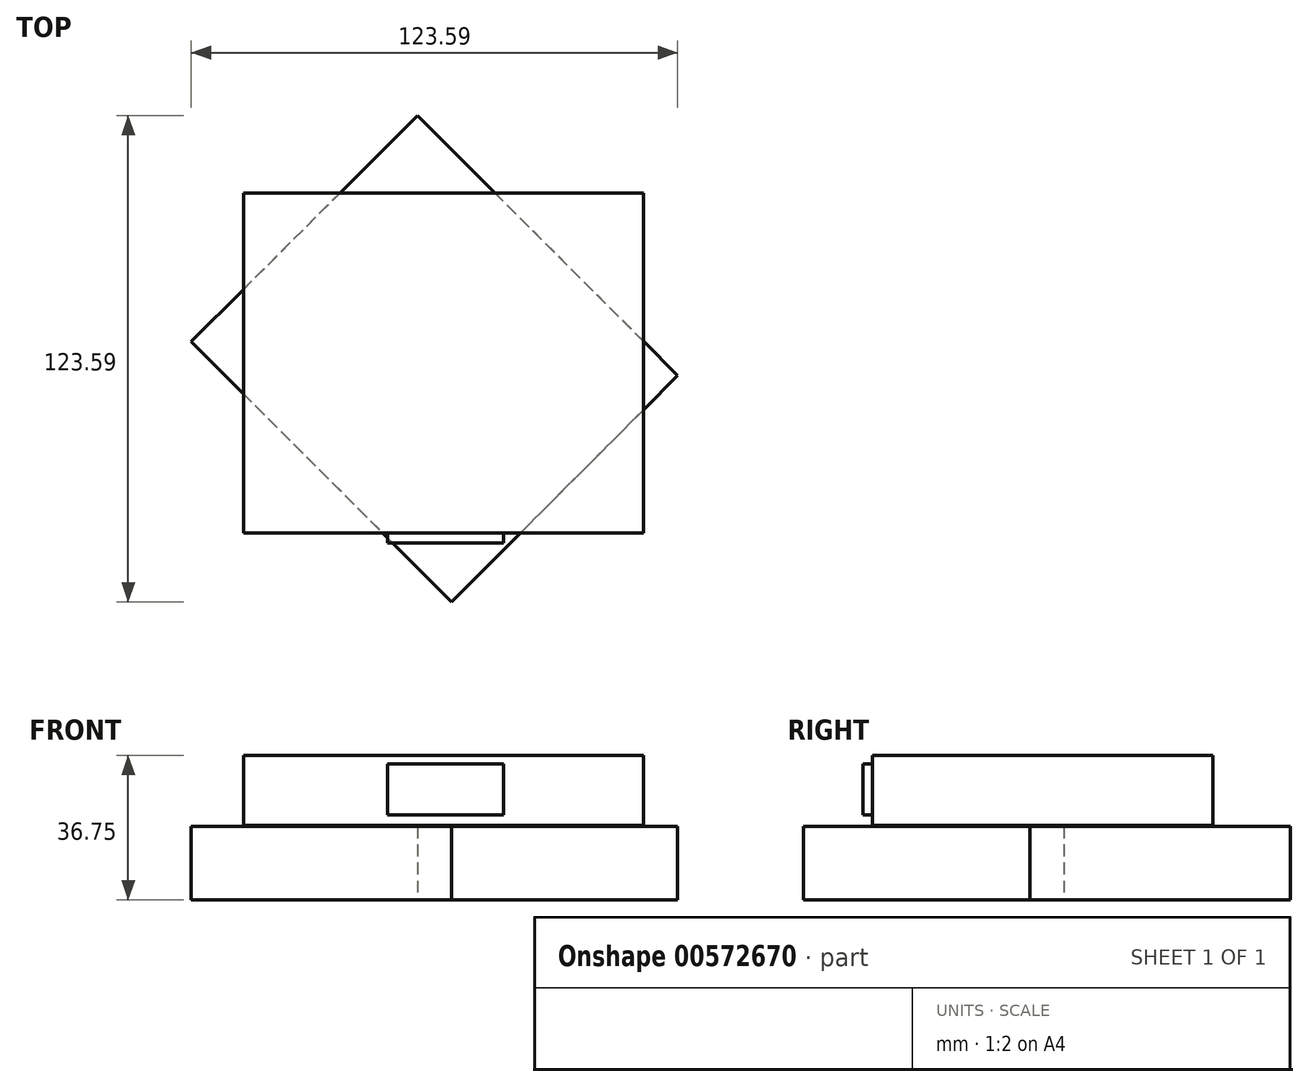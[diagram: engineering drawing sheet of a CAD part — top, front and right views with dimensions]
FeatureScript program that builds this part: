
annotation { "Feature Type Name" : "Feature", "Feature Type Description" : "" }
export const myFeature = defineFeature(function(context is Context, id is Id, definition is map)
    precondition{}
    {
        {
            var Q0;
            Q0=qCreatedBy(makeId("Front.planeOp"),FACE);
            var sketch = newSketch(context, id + "F0", { "sketchPlane" : qUnion([Q0])});
            skLineSegment(sketch, "E0.bottom", {"start": v(-50.88, 9.26) * mm, "end": v(50.72, 9.26) * mm});
            skLineSegment(sketch, "E0.top", {"start": v(-50.88, -8.52) * mm, "end": v(50.72, -8.52) * mm});
            skLineSegment(sketch, "E0.left", {"start": v(-50.88, 9.26) * mm, "end": v(-50.88, -8.52) * mm});
            skLineSegment(sketch, "E0.right", {"start": v(50.72, 9.26) * mm, "end": v(50.72, -8.52) * mm});
            skLineSegment(sketch, "E1", {"start": v(-50.88, -8.52) * mm, "end": v(0, -8.52) * mm});
            skSolve(sketch);
        }
        {
            var Q0;
            Q0=makeQuery(id+"F0.imprint","IMPRINT",FACE,{"disambiguationData":[TD([[makeQuery(id+"F0.imprint","IMPRINT",EDGE,{"derivedFrom":sQuery(id+"F0.wireOp",EDGE,"E0.bottom")}),-1.0]])]});
            extrude(context, id + "F1", {"entities" : qUnion([Q0]), "endBound" : BoundingType.SYMMETRIC, "depth" : 88.9 * mm, "offsetDistance" : 25.4 * mm});
        }
        {
            var Q0;
            Q0=makeQuery(id+"F1.opExtrude","CAP_FACE",FACE,{"disambiguationData":[OSD([sQuery(id+"F0.wireOp",EDGE,"E0.bottom"),sQuery(id+"F0.wireOp",EDGE,"E0.top"),sQuery(id+"F0.wireOp",EDGE,"E0.left"),sQuery(id+"F0.wireOp",EDGE,"E0.right"),sQuery(id+"F0.wireOp",EDGE,"E1")])],"isStart":false});
            var sketch = newSketch(context, id + "F2", { "sketchPlane" : qUnion([Q0])});
            skLineSegment(sketch, "E2.bottom", {"start": v(-14.24, 7.12) * mm, "end": v(15.26, 7.12) * mm});
            skLineSegment(sketch, "E2.top", {"start": v(-14.24, -5.88) * mm, "end": v(15.26, -5.88) * mm});
            skLineSegment(sketch, "E2.left", {"start": v(-14.24, 7.12) * mm, "end": v(-14.24, -5.88) * mm});
            skLineSegment(sketch, "E2.right", {"start": v(15.26, 7.12) * mm, "end": v(15.26, -5.88) * mm});
            skSolve(sketch);
        }
        {
            var Q0;
            Q0=makeQuery(id+"F2.imprint","IMPRINT",FACE,{"disambiguationData":[TD([[makeQuery(id+"F2.imprint","IMPRINT",EDGE,{"derivedFrom":sQuery(id+"F2.wireOp",EDGE,"E2.bottom")}),1.0]])]});
            extrude(context, id + "F3", {"entities" : qUnion([Q0]), "operationType" : NewBodyOperationType.REMOVE, "endBound" : BoundingType.SYMMETRIC, "oppositeDirection" : true, "depth" : 5 * mm, "offsetDistance" : 25.4 * mm});
        }
        {
            var Q0;
            Q0=qCreatedBy(makeId("Front.planeOp"),FACE);
            var Q1;
            Q1=qCreatedBy(makeId("Right.planeOp"),FACE);
            cPlane(context, id + "F4", {"entities" : qUnion([Q0, Q1]), "cplaneType" : CPlaneType.MID_PLANE, "offset" : 25.4 * mm, "width" : 152.4 * mm, "height" : 152.4 * mm});
        }
        {
            var Q0;
            Q0=qCreatedBy(id+"F4.planeOp",FACE);
            var sketch = newSketch(context, id + "F5", { "sketchPlane" : qUnion([Q0])});
            skLineSegment(sketch, "E3.bottom", {"start": v(-50.05, -8.78) * mm, "end": v(43.46, -8.78) * mm});
            skLineSegment(sketch, "E3.top", {"start": v(-50.05, -27.5) * mm, "end": v(43.46, -27.5) * mm});
            skLineSegment(sketch, "E3.left", {"start": v(-50.05, -8.78) * mm, "end": v(-50.05, -27.5) * mm});
            skLineSegment(sketch, "E3.right", {"start": v(43.46, -8.78) * mm, "end": v(43.46, -27.5) * mm});
            skSolve(sketch);
        }
        {
            var Q0;
            Q0=makeQuery(id+"F5.imprint","IMPRINT",FACE,{"disambiguationData":[TD([[makeQuery(id+"F5.imprint","IMPRINT",EDGE,{"derivedFrom":sQuery(id+"F5.wireOp",EDGE,"E3.bottom")}),-1.0]])]});
            extrude(context, id + "F6", {"entities" : qUnion([Q0]), "endBound" : BoundingType.SYMMETRIC, "depth" : 81.28 * mm, "offsetDistance" : 25.4 * mm});
        }
    });
